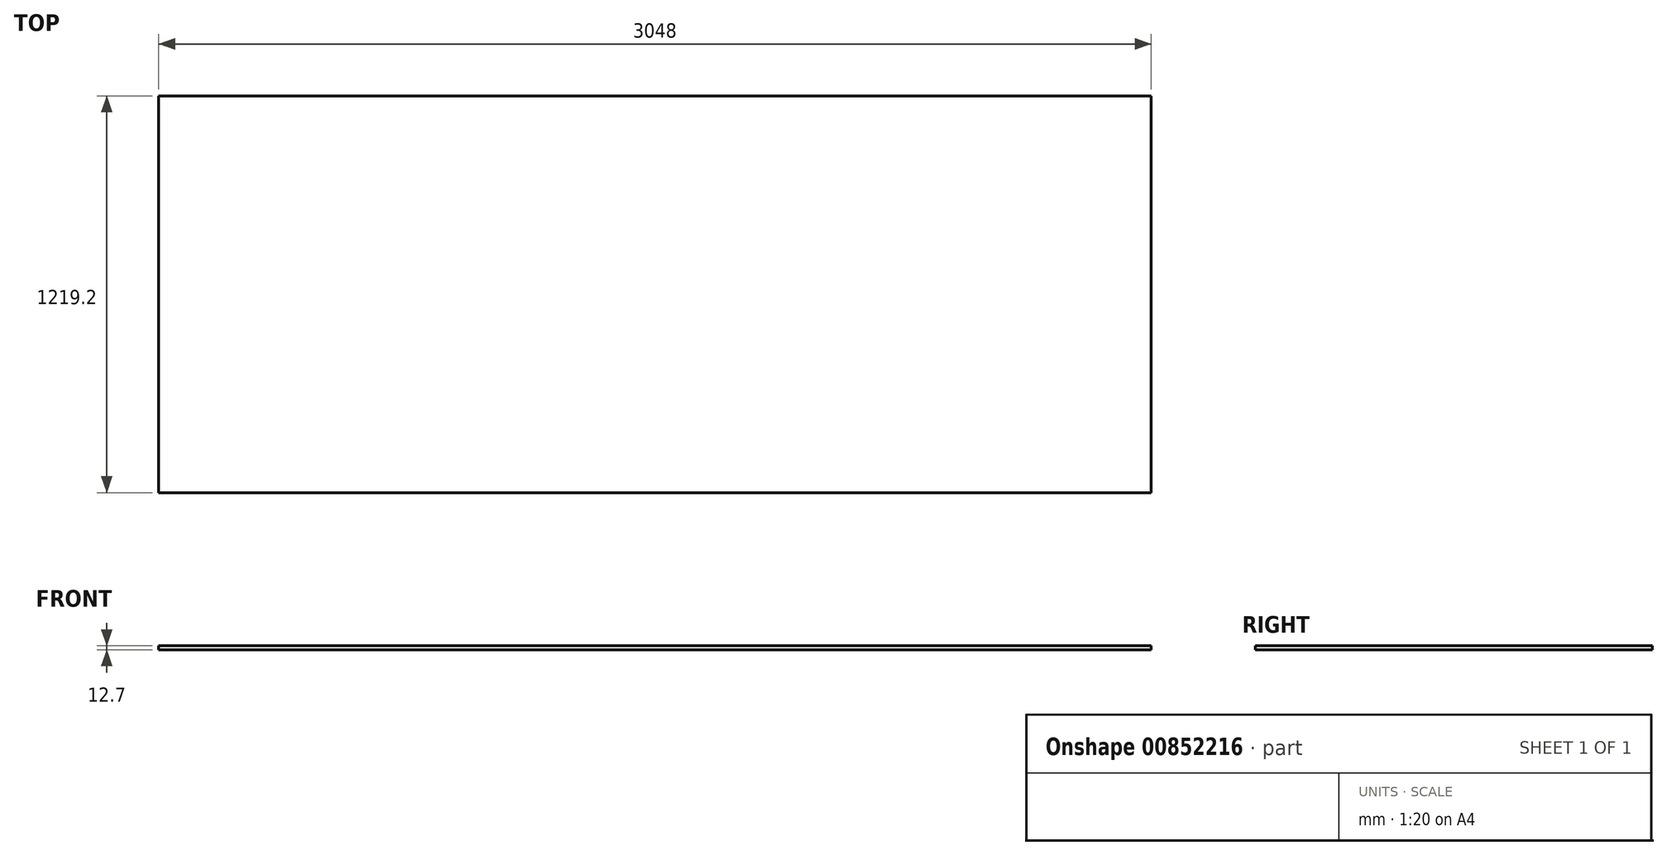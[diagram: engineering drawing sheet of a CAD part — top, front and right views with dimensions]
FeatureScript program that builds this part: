
annotation { "Feature Type Name" : "Feature", "Feature Type Description" : "" }
export const myFeature = defineFeature(function(context is Context, id is Id, definition is map)
    precondition{}
    {
        {
            var Q0;
            Q0=qCreatedBy(makeId("Top.planeOp"),FACE);
            var sketch = newSketch(context, id + "F0", { "sketchPlane" : qUnion([Q0])});
            skLineSegment(sketch, "E0.bottom", {"start": v(-1524, -609.6) * mm, "end": v(1524, -609.6) * mm});
            skLineSegment(sketch, "E0.top", {"start": v(-1524, 609.6) * mm, "end": v(1524, 609.6) * mm});
            skLineSegment(sketch, "E0.left", {"start": v(-1524, -609.6) * mm, "end": v(-1524, 609.6) * mm});
            skLineSegment(sketch, "E0.right", {"start": v(1524, -609.6) * mm, "end": v(1524, 609.6) * mm});
            skPoint(sketch, "E0.middle", {"position": v(0, 0) * mm});
            skSolve(sketch);
        }
        {
            var Q0;
            Q0 = qSketchRegion(id + "F0", true);
            extrude(context, id + "F1", {"entities" : qUnion([Q0]), "depth" : 12.7 * mm, "offsetDistance" : 25.4 * mm});
        }
    });
